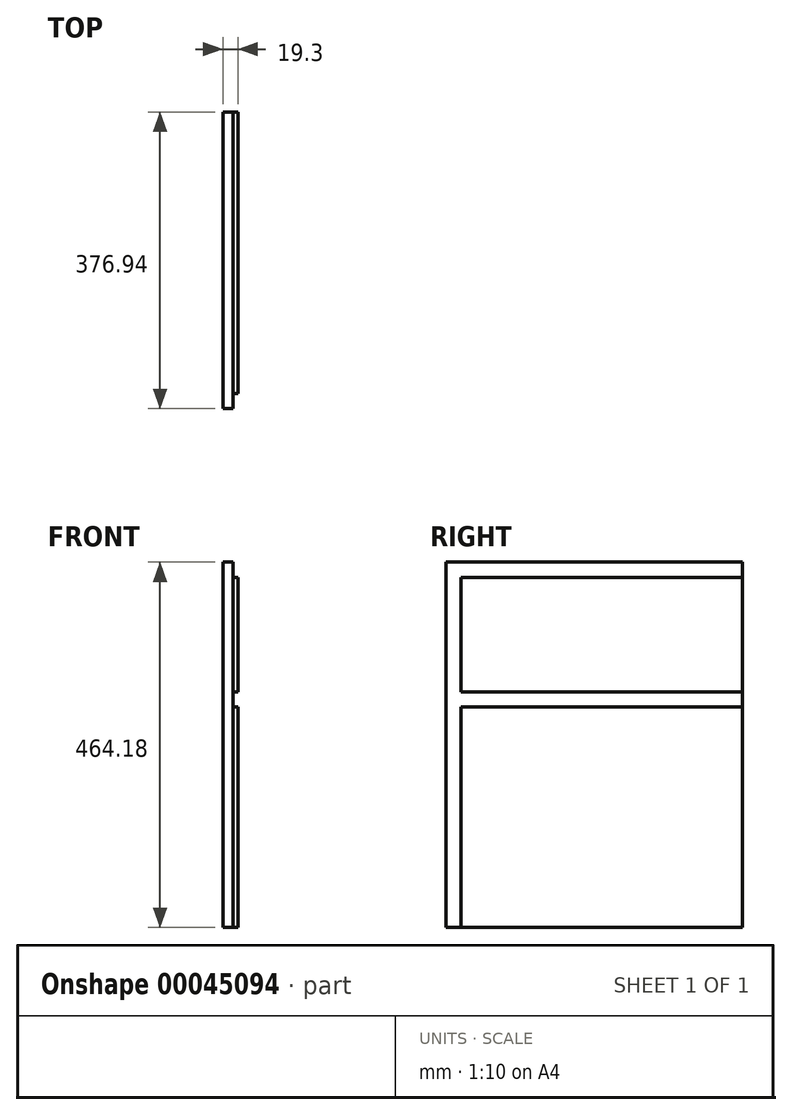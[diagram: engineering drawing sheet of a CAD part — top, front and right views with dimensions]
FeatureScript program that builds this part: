
annotation { "Feature Type Name" : "Feature", "Feature Type Description" : "" }
export const myFeature = defineFeature(function(context is Context, id is Id, definition is map)
    precondition{}
    {
        {
            var Q0;
            Q0=qCreatedBy(makeId("Right.planeOp"),FACE);
            var sketch = newSketch(context, id + "F0", { "sketchPlane" : qUnion([Q0])});
            skLineSegment(sketch, "E0.rect.bottom", {"start": v(-188.47, 232.1) * mm, "end": v(188.47, 232.1) * mm});
            skLineSegment(sketch, "E0.rect.top", {"start": v(-188.47, -232.1) * mm, "end": v(188.47, -232.1) * mm});
            skLineSegment(sketch, "E0.rect.left", {"start": v(-188.47, 232.1) * mm, "end": v(-188.47, -232.1) * mm});
            skLineSegment(sketch, "E0.rect.right", {"start": v(188.47, 232.1) * mm, "end": v(188.47, -232.1) * mm});
            skPoint(sketch, "E0.rect.middle", {"position": v(0, 0) * mm});
            skSolve(sketch);
        }
        {
            var Q0;
            Q0=qSketchRegion(id+"F0",true);
            extrude(context, id + "F1", {"entities" : qUnion([Q0]), "depth" : 19.3 * mm});
        }
        {
            var Q0;
            Q0=makeQuery(id+"F1.opExtrude","CAP_FACE",FACE,{"disambiguationData":[OSD([sQuery(id+"F0.wireOp",EDGE,"E0.rect.bottom"),sQuery(id+"F0.wireOp",EDGE,"E0.rect.top"),sQuery(id+"F0.wireOp",EDGE,"E0.rect.left"),sQuery(id+"F0.wireOp",EDGE,"E0.rect.right")])],"isStart":false});
            var sketch = newSketch(context, id + "F2", { "sketchPlane" : qUnion([Q0])});
            skLineSegment(sketch, "E1.bottom", {"start": v(-188.47, 67.37) * mm, "end": v(188.47, 67.37) * mm});
            skLineSegment(sketch, "E1.top", {"start": v(-188.47, 48.07) * mm, "end": v(188.47, 48.07) * mm});
            skLineSegment(sketch, "E1.left", {"start": v(-188.47, 67.37) * mm, "end": v(-188.47, 48.07) * mm});
            skLineSegment(sketch, "E1.right", {"start": v(188.47, 67.37) * mm, "end": v(188.47, 48.07) * mm});
            skLineSegment(sketch, "E2.bottom", {"start": v(-188.47, 232.1) * mm, "end": v(-169.16, 232.1) * mm});
            skLineSegment(sketch, "E2.top", {"start": v(-188.47, -232.1) * mm, "end": v(-169.16, -232.1) * mm});
            skLineSegment(sketch, "E2.left", {"start": v(-188.47, 232.1) * mm, "end": v(-188.47, -232.1) * mm});
            skLineSegment(sketch, "E2.right", {"start": v(-169.16, 232.1) * mm, "end": v(-169.16, -232.1) * mm});
            skLineSegment(sketch, "E3.bottom", {"start": v(188.47, 232.1) * mm, "end": v(-188.47, 232.1) * mm});
            skLineSegment(sketch, "E3.top", {"start": v(188.47, 212.79) * mm, "end": v(-188.47, 212.79) * mm});
            skLineSegment(sketch, "E3.left", {"start": v(188.47, 232.1) * mm, "end": v(188.47, 212.79) * mm});
            skLineSegment(sketch, "E3.right", {"start": v(-188.47, 232.1) * mm, "end": v(-188.47, 212.79) * mm});
            skSolve(sketch);
        }
        {
            var Q0;
            Q0=qSketchRegion(id+"F2",true);
            extrude(context, id + "F3", {"entities" : qUnion([Q0]), "operationType" : NewBodyOperationType.REMOVE, "oppositeDirection" : true, "depth" : 6.35 * mm});
        }
    });
